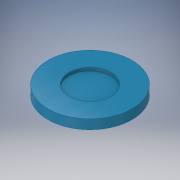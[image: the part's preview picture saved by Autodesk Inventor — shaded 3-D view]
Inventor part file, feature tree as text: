
AUTODESK INVENTOR PART (.ipt)
format: ipt  version: 2018 (Build 220112000, 112)  size: 105,472 bytes
history: native  units: in
note: dims shown in document units (in); Inventor stores cm internally (conversion verified against a paired STEP export)
features: extrude x2, sketch x2
ambient origin geometry x8: Origin, YZ Plane, XZ Plane, XY Plane, X Axis, Y Axis, Z Axis, Center Point
bodies: Solid1 (feature_tree)
feature tree (4):
  extrude  "Extrusion1"  Depth=0.3543in TaperAngle=0.0deg
  extrude  "Extrusion3"  Depth=0.1181in TaperAngle=0.0deg
  sketch  "Sketch1"  dims[d0=3.1496in d1=0.3543in d2=0.0in]
  sketch  "Sketch3"  dims[d6=1.5748in d7=0.1181in d8=0.0in]
